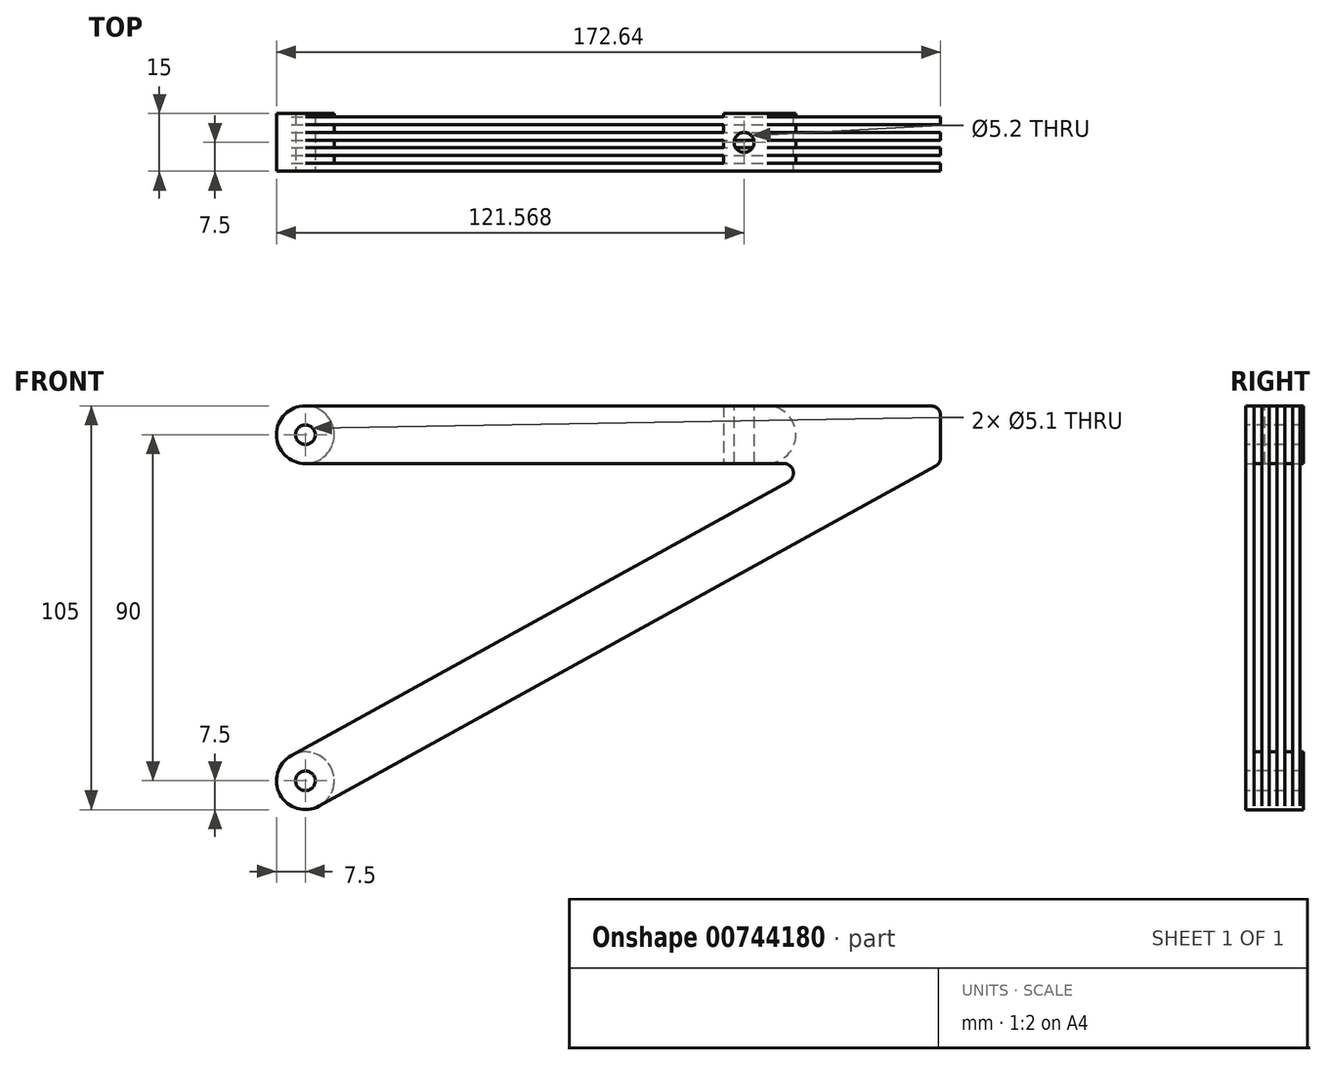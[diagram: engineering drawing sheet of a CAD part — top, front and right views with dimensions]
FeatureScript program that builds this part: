
annotation { "Feature Type Name" : "Feature", "Feature Type Description" : "" }
export const myFeature = defineFeature(function(context is Context, id is Id, definition is map)
    precondition{}
    {
        {
            var Q0;
            Q0=qCreatedBy(makeId("Front.planeOp"),FACE);
            var sketch = newSketch(context, id + "F0", { "sketchPlane" : qUnion([Q0])});
            skLineSegment(sketch, "E0", {"start": v(0, 120) * mm, "end": v(0, 30) * mm, "construction": true});
            skCircle(sketch, "E1", {"center": v(0, 120) * mm, "radius": 7.5 * mm});
            skCircle(sketch, "E2", {"center": v(0, 30) * mm, "radius": 7.5 * mm});
            skLineSegment(sketch, "E3", {"start": v(0, 127.5) * mm, "end": v(120, 127.5) * mm});
            skLineSegment(sketch, "E4", {"start": v(0, 112.5) * mm, "end": v(120, 112.5) * mm});
            skArc(sketch, "E5", {"start": v(120, 112.5) * mm, "mid": v(127.5, 120) * mm, "end": v(120, 127.5) * mm});
            skLineSegment(sketch, "E6", {"start": v(120, 127.5) * mm, "end": v(162.64, 127.5) * mm});
            skLineSegment(sketch, "E7", {"start": v(165.14, 125) * mm, "end": v(165.14, 113.98) * mm});
            skLineSegment(sketch, "E8", {"start": v(124.36, 112.5) * mm, "end": v(120, 112.5) * mm});
            skLineSegment(sketch, "E9", {"start": v(125.57, 107.81) * mm, "end": v(-3.62, 36.57) * mm});
            skLineSegment(sketch, "E10", {"start": v(3.62, 23.43) * mm, "end": v(163.85, 111.79) * mm});
            skPoint(sketch, "E11.visualSharp", {"position": v(165.14, 127.5) * mm});
            skArc(sketch, "E11.filletArc", {"start": v(165.14, 125) * mm, "mid": v(164.4, 126.77) * mm, "end": v(162.64, 127.5) * mm});
            skPoint(sketch, "E12.visualSharp", {"position": v(165.14, 112.5) * mm});
            skArc(sketch, "E12.filletArc", {"start": v(163.85, 111.79) * mm, "mid": v(164.8, 112.7) * mm, "end": v(165.14, 113.98) * mm});
            skPoint(sketch, "E13.visualSharp", {"position": v(134.08, 112.5) * mm});
            skArc(sketch, "E13.filletArc", {"start": v(125.57, 107.81) * mm, "mid": v(126.79, 110.62) * mm, "end": v(124.36, 112.5) * mm});
            skLineSegment(sketch, "E14", {"start": v(108.79, 127.5) * mm, "end": v(108.79, 112.5) * mm});
            skSolve(sketch);
        }
        {
            var Q0;
            {var subQ0=sQuery(id+"F0.wireOp",EDGE,"E3");Q0=makeQuery(id+"F0.imprint","IMPRINT",FACE,{"disambiguationData":[TD([[makeQuery(id+"F0.imprint","IMPRINT",EDGE,{"derivedFrom":subQ0}),-1.0]])]});}
            var Q1;
            {var subQ0=sQuery(id+"F0.wireOp",EDGE,"E1");var subQ1=makeQuery(id+"F0.imprint","INTERSECT",VERTEX,{"derivedFrom":[subQ0,sQuery(id+"F0.wireOp",EDGE,"E3")]});Q1=makeQuery(id+"F0.imprint","IMPRINT",FACE,{"disambiguationData":[TD([[makeQuery(id+"F0.imprint","IMPRINT",EDGE,{"disambiguationData":[TD([[subQ1,-1.0]])],"derivedFrom":subQ0}),1.0]])]});}
            var Q2;
            {var subQ3=sQuery(id+"F0.wireOp",EDGE,"E6");Q2=makeQuery(id+"F0.imprint","IMPRINT",FACE,{"disambiguationData":[TD([[makeQuery(id+"F0.imprint","IMPRINT",EDGE,{"derivedFrom":subQ3}),-1.0]])]});}
            var Q3;
            {var subQ0=sQuery(id+"F0.wireOp",EDGE,"E9");Q3=makeQuery(id+"F0.imprint","IMPRINT",FACE,{"disambiguationData":[TD([[makeQuery(id+"F0.imprint","IMPRINT",EDGE,{"derivedFrom":subQ0}),1.0]])]});}
            var Q4;
            {var subQ0=sQuery(id+"F0.wireOp",EDGE,"E2");var subQ1=makeQuery(id+"F0.imprint","INTERSECT",VERTEX,{"derivedFrom":[subQ0,sQuery(id+"F0.wireOp",EDGE,"E9")]});Q4=makeQuery(id+"F0.imprint","IMPRINT",FACE,{"disambiguationData":[TD([[makeQuery(id+"F0.imprint","IMPRINT",EDGE,{"disambiguationData":[TD([[subQ1,-1.0]])],"derivedFrom":subQ0}),1.0]])]});}
            var Q5;
            {var subQ0=sQuery(id+"F0.wireOp",EDGE,"E5");var subQ1=makeQuery(id+"F0.imprint","INTERSECT",VERTEX,{"derivedFrom":[sQuery(id+"F0.wireOp",EDGE,"E3"),subQ0,sQuery(id+"F0.wireOp",EDGE,"E6")]});Q5=makeQuery(id+"F0.imprint","IMPRINT",FACE,{"disambiguationData":[TD([[makeQuery(id+"F0.imprint","IMPRINT",EDGE,{"disambiguationData":[TD([[subQ1,-1.0]])],"derivedFrom":subQ0}),1.0]])]});}
            extrude(context, id + "F1", {"entities" : qUnion([Q0, Q1, Q2, Q3, Q4, Q5]), "depth" : 15 * mm, "offsetDistance" : 25 * mm, "symmetric" : true});
        }
        {
            var Q0;
            Q0=qCreatedBy(makeId("Top.planeOp"),FACE);
            var sketch = newSketch(context, id + "F2", { "sketchPlane" : qUnion([Q0])});
            skLineSegment(sketch, "E15.bottom", {"start": v(-14.24, 8.62) * mm, "end": v(173.7, 8.62) * mm});
            skLineSegment(sketch, "E15.top", {"start": v(-14.24, 6.62) * mm, "end": v(173.7, 6.62) * mm});
            skLineSegment(sketch, "E15.left", {"start": v(-14.24, 8.62) * mm, "end": v(-14.24, 6.62) * mm});
            skLineSegment(sketch, "E15.right", {"start": v(173.7, 8.62) * mm, "end": v(173.7, 6.62) * mm});
            skLineSegment(sketch, "E16.1.0.0", {"start": v(10.76, 8.62) * mm, "end": v(198.7, 8.62) * mm});
            skLineSegment(sketch, "E16.1.0.1", {"start": v(10.76, 6.62) * mm, "end": v(198.7, 6.62) * mm});
            skLineSegment(sketch, "E16.1.0.2", {"start": v(198.7, 8.62) * mm, "end": v(198.7, 6.62) * mm});
            skLineSegment(sketch, "E16.1.0.3", {"start": v(10.76, 8.62) * mm, "end": v(10.76, 6.62) * mm});
            skLineSegment(sketch, "E16.2.0.0", {"start": v(35.76, 8.62) * mm, "end": v(223.7, 8.62) * mm});
            skLineSegment(sketch, "E16.2.0.1", {"start": v(35.76, 6.62) * mm, "end": v(223.7, 6.62) * mm});
            skLineSegment(sketch, "E16.2.0.2", {"start": v(223.7, 8.62) * mm, "end": v(223.7, 6.62) * mm});
            skLineSegment(sketch, "E16.2.0.3", {"start": v(35.76, 8.62) * mm, "end": v(35.76, 6.62) * mm});
            skLineSegment(sketch, "E16.direction1", {"start": v(-14.24, 6.62) * mm, "end": v(10.76, 6.62) * mm, "construction": true});
            skLineSegment(sketch, "E17.0.1.0", {"start": v(10.76, 2.62) * mm, "end": v(198.7, 2.62) * mm});
            skLineSegment(sketch, "E17.0.1.1", {"start": v(35.76, 4.62) * mm, "end": v(223.7, 4.62) * mm});
            skLineSegment(sketch, "E17.0.1.2", {"start": v(-14.24, 4.62) * mm, "end": v(173.7, 4.62) * mm});
            skLineSegment(sketch, "E17.0.1.3", {"start": v(-14.24, 2.62) * mm, "end": v(10.76, 2.62) * mm, "construction": true});
            skLineSegment(sketch, "E17.0.1.4", {"start": v(10.76, 4.62) * mm, "end": v(198.7, 4.62) * mm});
            skLineSegment(sketch, "E17.0.1.5", {"start": v(35.76, 2.62) * mm, "end": v(223.7, 2.62) * mm});
            skLineSegment(sketch, "E17.0.1.6", {"start": v(-14.24, 2.62) * mm, "end": v(173.7, 2.62) * mm});
            skLineSegment(sketch, "E17.0.1.7", {"start": v(35.76, 4.62) * mm, "end": v(35.76, 2.62) * mm});
            skLineSegment(sketch, "E17.0.1.8", {"start": v(-14.24, 4.62) * mm, "end": v(-14.24, 2.62) * mm});
            skLineSegment(sketch, "E17.0.1.9", {"start": v(223.7, 4.62) * mm, "end": v(223.7, 2.62) * mm});
            skLineSegment(sketch, "E17.0.1.10", {"start": v(198.7, 4.62) * mm, "end": v(198.7, 2.62) * mm});
            skLineSegment(sketch, "E17.0.1.11", {"start": v(173.7, 4.62) * mm, "end": v(173.7, 2.62) * mm});
            skLineSegment(sketch, "E17.0.1.12", {"start": v(10.76, 4.62) * mm, "end": v(10.76, 2.62) * mm});
            skLineSegment(sketch, "E17.0.2.0", {"start": v(10.76, -1.38) * mm, "end": v(198.7, -1.38) * mm});
            skLineSegment(sketch, "E17.0.2.1", {"start": v(35.76, 0.62) * mm, "end": v(223.7, 0.62) * mm});
            skLineSegment(sketch, "E17.0.2.2", {"start": v(-14.24, 0.62) * mm, "end": v(173.7, 0.62) * mm});
            skLineSegment(sketch, "E17.0.2.3", {"start": v(-14.24, -1.38) * mm, "end": v(10.76, -1.38) * mm, "construction": true});
            skLineSegment(sketch, "E17.0.2.4", {"start": v(10.76, 0.62) * mm, "end": v(198.7, 0.62) * mm});
            skLineSegment(sketch, "E17.0.2.5", {"start": v(35.76, -1.38) * mm, "end": v(223.7, -1.38) * mm});
            skLineSegment(sketch, "E17.0.2.6", {"start": v(-14.24, -1.38) * mm, "end": v(173.7, -1.38) * mm});
            skLineSegment(sketch, "E17.0.2.7", {"start": v(35.76, 0.62) * mm, "end": v(35.76, -1.38) * mm});
            skLineSegment(sketch, "E17.0.2.8", {"start": v(-14.24, 0.62) * mm, "end": v(-14.24, -1.38) * mm});
            skLineSegment(sketch, "E17.0.2.9", {"start": v(223.7, 0.62) * mm, "end": v(223.7, -1.38) * mm});
            skLineSegment(sketch, "E17.0.2.10", {"start": v(198.7, 0.62) * mm, "end": v(198.7, -1.38) * mm});
            skLineSegment(sketch, "E17.0.2.11", {"start": v(173.7, 0.62) * mm, "end": v(173.7, -1.38) * mm});
            skLineSegment(sketch, "E17.0.2.12", {"start": v(10.76, 0.62) * mm, "end": v(10.76, -1.38) * mm});
            skLineSegment(sketch, "E17.0.3.0", {"start": v(10.76, -5.38) * mm, "end": v(198.7, -5.38) * mm});
            skLineSegment(sketch, "E17.0.3.1", {"start": v(35.76, -3.38) * mm, "end": v(223.7, -3.38) * mm});
            skLineSegment(sketch, "E17.0.3.2", {"start": v(-14.24, -3.38) * mm, "end": v(173.7, -3.38) * mm});
            skLineSegment(sketch, "E17.0.3.3", {"start": v(-14.24, -5.38) * mm, "end": v(10.76, -5.38) * mm, "construction": true});
            skLineSegment(sketch, "E17.0.3.4", {"start": v(10.76, -3.38) * mm, "end": v(198.7, -3.38) * mm});
            skLineSegment(sketch, "E17.0.3.5", {"start": v(35.76, -5.38) * mm, "end": v(223.7, -5.38) * mm});
            skLineSegment(sketch, "E17.0.3.6", {"start": v(-14.24, -5.38) * mm, "end": v(173.7, -5.38) * mm});
            skLineSegment(sketch, "E17.0.3.7", {"start": v(35.76, -3.38) * mm, "end": v(35.76, -5.38) * mm});
            skLineSegment(sketch, "E17.0.3.8", {"start": v(-14.24, -3.38) * mm, "end": v(-14.24, -5.38) * mm});
            skLineSegment(sketch, "E17.0.3.9", {"start": v(223.7, -3.38) * mm, "end": v(223.7, -5.38) * mm});
            skLineSegment(sketch, "E17.0.3.10", {"start": v(198.7, -3.38) * mm, "end": v(198.7, -5.38) * mm});
            skLineSegment(sketch, "E17.0.3.11", {"start": v(173.7, -3.38) * mm, "end": v(173.7, -5.38) * mm});
            skLineSegment(sketch, "E17.0.3.12", {"start": v(10.76, -3.38) * mm, "end": v(10.76, -5.38) * mm});
            skLineSegment(sketch, "E17.1.0.1", {"start": v(60.76, 8.62) * mm, "end": v(248.7, 8.62) * mm});
            skLineSegment(sketch, "E17.1.0.3", {"start": v(10.76, 6.62) * mm, "end": v(35.76, 6.62) * mm, "construction": true});
            skLineSegment(sketch, "E17.1.0.5", {"start": v(60.76, 6.62) * mm, "end": v(248.7, 6.62) * mm});
            skLineSegment(sketch, "E17.1.0.7", {"start": v(60.76, 8.62) * mm, "end": v(60.76, 6.62) * mm});
            skLineSegment(sketch, "E17.1.0.9", {"start": v(248.7, 8.62) * mm, "end": v(248.7, 6.62) * mm});
            skLineSegment(sketch, "E17.1.1.0", {"start": v(35.76, 2.62) * mm, "end": v(223.7, 2.62) * mm});
            skLineSegment(sketch, "E17.1.1.1", {"start": v(60.76, 4.62) * mm, "end": v(248.7, 4.62) * mm});
            skLineSegment(sketch, "E17.1.1.2", {"start": v(10.76, 4.62) * mm, "end": v(198.7, 4.62) * mm});
            skLineSegment(sketch, "E17.1.1.3", {"start": v(10.76, 2.62) * mm, "end": v(35.76, 2.62) * mm, "construction": true});
            skLineSegment(sketch, "E17.1.1.4", {"start": v(35.76, 4.62) * mm, "end": v(223.7, 4.62) * mm});
            skLineSegment(sketch, "E17.1.1.5", {"start": v(60.76, 2.62) * mm, "end": v(248.7, 2.62) * mm});
            skLineSegment(sketch, "E17.1.1.6", {"start": v(10.76, 2.62) * mm, "end": v(198.7, 2.62) * mm});
            skLineSegment(sketch, "E17.1.1.7", {"start": v(60.76, 4.62) * mm, "end": v(60.76, 2.62) * mm});
            skLineSegment(sketch, "E17.1.1.8", {"start": v(10.76, 4.62) * mm, "end": v(10.76, 2.62) * mm});
            skLineSegment(sketch, "E17.1.1.9", {"start": v(248.7, 4.62) * mm, "end": v(248.7, 2.62) * mm});
            skLineSegment(sketch, "E17.1.1.10", {"start": v(223.7, 4.62) * mm, "end": v(223.7, 2.62) * mm});
            skLineSegment(sketch, "E17.1.1.11", {"start": v(198.7, 4.62) * mm, "end": v(198.7, 2.62) * mm});
            skLineSegment(sketch, "E17.1.1.12", {"start": v(35.76, 4.62) * mm, "end": v(35.76, 2.62) * mm});
            skLineSegment(sketch, "E17.1.2.0", {"start": v(35.76, -1.38) * mm, "end": v(223.7, -1.38) * mm});
            skLineSegment(sketch, "E17.1.2.1", {"start": v(60.76, 0.62) * mm, "end": v(248.7, 0.62) * mm});
            skLineSegment(sketch, "E17.1.2.2", {"start": v(10.76, 0.62) * mm, "end": v(198.7, 0.62) * mm});
            skLineSegment(sketch, "E17.1.2.3", {"start": v(10.76, -1.38) * mm, "end": v(35.76, -1.38) * mm, "construction": true});
            skLineSegment(sketch, "E17.1.2.4", {"start": v(35.76, 0.62) * mm, "end": v(223.7, 0.62) * mm});
            skLineSegment(sketch, "E17.1.2.5", {"start": v(60.76, -1.38) * mm, "end": v(248.7, -1.38) * mm});
            skLineSegment(sketch, "E17.1.2.6", {"start": v(10.76, -1.38) * mm, "end": v(198.7, -1.38) * mm});
            skLineSegment(sketch, "E17.1.2.7", {"start": v(60.76, 0.62) * mm, "end": v(60.76, -1.38) * mm});
            skLineSegment(sketch, "E17.1.2.8", {"start": v(10.76, 0.62) * mm, "end": v(10.76, -1.38) * mm});
            skLineSegment(sketch, "E17.1.2.9", {"start": v(248.7, 0.62) * mm, "end": v(248.7, -1.38) * mm});
            skLineSegment(sketch, "E17.1.2.10", {"start": v(223.7, 0.62) * mm, "end": v(223.7, -1.38) * mm});
            skLineSegment(sketch, "E17.1.2.11", {"start": v(198.7, 0.62) * mm, "end": v(198.7, -1.38) * mm});
            skLineSegment(sketch, "E17.1.2.12", {"start": v(35.76, 0.62) * mm, "end": v(35.76, -1.38) * mm});
            skLineSegment(sketch, "E17.1.3.0", {"start": v(35.76, -5.38) * mm, "end": v(223.7, -5.38) * mm});
            skLineSegment(sketch, "E17.1.3.1", {"start": v(60.76, -3.38) * mm, "end": v(248.7, -3.38) * mm});
            skLineSegment(sketch, "E17.1.3.2", {"start": v(10.76, -3.38) * mm, "end": v(198.7, -3.38) * mm});
            skLineSegment(sketch, "E17.1.3.3", {"start": v(10.76, -5.38) * mm, "end": v(35.76, -5.38) * mm, "construction": true});
            skLineSegment(sketch, "E17.1.3.4", {"start": v(35.76, -3.38) * mm, "end": v(223.7, -3.38) * mm});
            skLineSegment(sketch, "E17.1.3.5", {"start": v(60.76, -5.38) * mm, "end": v(248.7, -5.38) * mm});
            skLineSegment(sketch, "E17.1.3.6", {"start": v(10.76, -5.38) * mm, "end": v(198.7, -5.38) * mm});
            skLineSegment(sketch, "E17.1.3.7", {"start": v(60.76, -3.38) * mm, "end": v(60.76, -5.38) * mm});
            skLineSegment(sketch, "E17.1.3.8", {"start": v(10.76, -3.38) * mm, "end": v(10.76, -5.38) * mm});
            skLineSegment(sketch, "E17.1.3.9", {"start": v(248.7, -3.38) * mm, "end": v(248.7, -5.38) * mm});
            skLineSegment(sketch, "E17.1.3.10", {"start": v(223.7, -3.38) * mm, "end": v(223.7, -5.38) * mm});
            skLineSegment(sketch, "E17.1.3.11", {"start": v(198.7, -3.38) * mm, "end": v(198.7, -5.38) * mm});
            skLineSegment(sketch, "E17.1.3.12", {"start": v(35.76, -3.38) * mm, "end": v(35.76, -5.38) * mm});
            skLineSegment(sketch, "E17.2.0.0", {"start": v(60.76, 6.62) * mm, "end": v(248.7, 6.62) * mm});
            skLineSegment(sketch, "E17.2.0.1", {"start": v(85.76, 8.62) * mm, "end": v(273.7, 8.62) * mm});
            skLineSegment(sketch, "E17.2.0.3", {"start": v(35.76, 6.62) * mm, "end": v(60.76, 6.62) * mm, "construction": true});
            skLineSegment(sketch, "E17.2.0.4", {"start": v(60.76, 8.62) * mm, "end": v(248.7, 8.62) * mm});
            skLineSegment(sketch, "E17.2.0.5", {"start": v(85.76, 6.62) * mm, "end": v(273.7, 6.62) * mm});
            skLineSegment(sketch, "E17.2.0.7", {"start": v(85.76, 8.62) * mm, "end": v(85.76, 6.62) * mm});
            skLineSegment(sketch, "E17.2.0.9", {"start": v(273.7, 8.62) * mm, "end": v(273.7, 6.62) * mm});
            skLineSegment(sketch, "E17.2.0.10", {"start": v(248.7, 8.62) * mm, "end": v(248.7, 6.62) * mm});
            skLineSegment(sketch, "E17.2.0.12", {"start": v(60.76, 8.62) * mm, "end": v(60.76, 6.62) * mm});
            skLineSegment(sketch, "E17.2.1.0", {"start": v(60.76, 2.62) * mm, "end": v(248.7, 2.62) * mm});
            skLineSegment(sketch, "E17.2.1.1", {"start": v(85.76, 4.62) * mm, "end": v(273.7, 4.62) * mm});
            skLineSegment(sketch, "E17.2.1.2", {"start": v(35.76, 4.62) * mm, "end": v(223.7, 4.62) * mm});
            skLineSegment(sketch, "E17.2.1.3", {"start": v(35.76, 2.62) * mm, "end": v(60.76, 2.62) * mm, "construction": true});
            skLineSegment(sketch, "E17.2.1.4", {"start": v(60.76, 4.62) * mm, "end": v(248.7, 4.62) * mm});
            skLineSegment(sketch, "E17.2.1.5", {"start": v(85.76, 2.62) * mm, "end": v(273.7, 2.62) * mm});
            skLineSegment(sketch, "E17.2.1.6", {"start": v(35.76, 2.62) * mm, "end": v(223.7, 2.62) * mm});
            skLineSegment(sketch, "E17.2.1.7", {"start": v(85.76, 4.62) * mm, "end": v(85.76, 2.62) * mm});
            skLineSegment(sketch, "E17.2.1.8", {"start": v(35.76, 4.62) * mm, "end": v(35.76, 2.62) * mm});
            skLineSegment(sketch, "E17.2.1.9", {"start": v(273.7, 4.62) * mm, "end": v(273.7, 2.62) * mm});
            skLineSegment(sketch, "E17.2.1.10", {"start": v(248.7, 4.62) * mm, "end": v(248.7, 2.62) * mm});
            skLineSegment(sketch, "E17.2.1.11", {"start": v(223.7, 4.62) * mm, "end": v(223.7, 2.62) * mm});
            skLineSegment(sketch, "E17.2.1.12", {"start": v(60.76, 4.62) * mm, "end": v(60.76, 2.62) * mm});
            skLineSegment(sketch, "E17.2.2.0", {"start": v(60.76, -1.38) * mm, "end": v(248.7, -1.38) * mm});
            skLineSegment(sketch, "E17.2.2.1", {"start": v(85.76, 0.62) * mm, "end": v(273.7, 0.62) * mm});
            skLineSegment(sketch, "E17.2.2.2", {"start": v(35.76, 0.62) * mm, "end": v(223.7, 0.62) * mm});
            skLineSegment(sketch, "E17.2.2.3", {"start": v(35.76, -1.38) * mm, "end": v(60.76, -1.38) * mm, "construction": true});
            skLineSegment(sketch, "E17.2.2.4", {"start": v(60.76, 0.62) * mm, "end": v(248.7, 0.62) * mm});
            skLineSegment(sketch, "E17.2.2.5", {"start": v(85.76, -1.38) * mm, "end": v(273.7, -1.38) * mm});
            skLineSegment(sketch, "E17.2.2.6", {"start": v(35.76, -1.38) * mm, "end": v(223.7, -1.38) * mm});
            skLineSegment(sketch, "E17.2.2.7", {"start": v(85.76, 0.62) * mm, "end": v(85.76, -1.38) * mm});
            skLineSegment(sketch, "E17.2.2.8", {"start": v(35.76, 0.62) * mm, "end": v(35.76, -1.38) * mm});
            skLineSegment(sketch, "E17.2.2.9", {"start": v(273.7, 0.62) * mm, "end": v(273.7, -1.38) * mm});
            skLineSegment(sketch, "E17.2.2.10", {"start": v(248.7, 0.62) * mm, "end": v(248.7, -1.38) * mm});
            skLineSegment(sketch, "E17.2.2.11", {"start": v(223.7, 0.62) * mm, "end": v(223.7, -1.38) * mm});
            skLineSegment(sketch, "E17.2.2.12", {"start": v(60.76, 0.62) * mm, "end": v(60.76, -1.38) * mm});
            skLineSegment(sketch, "E17.2.3.0", {"start": v(60.76, -5.38) * mm, "end": v(248.7, -5.38) * mm});
            skLineSegment(sketch, "E17.2.3.1", {"start": v(85.76, -3.38) * mm, "end": v(273.7, -3.38) * mm});
            skLineSegment(sketch, "E17.2.3.2", {"start": v(35.76, -3.38) * mm, "end": v(223.7, -3.38) * mm});
            skLineSegment(sketch, "E17.2.3.3", {"start": v(35.76, -5.38) * mm, "end": v(60.76, -5.38) * mm, "construction": true});
            skLineSegment(sketch, "E17.2.3.4", {"start": v(60.76, -3.38) * mm, "end": v(248.7, -3.38) * mm});
            skLineSegment(sketch, "E17.2.3.5", {"start": v(85.76, -5.38) * mm, "end": v(273.7, -5.38) * mm});
            skLineSegment(sketch, "E17.2.3.6", {"start": v(35.76, -5.38) * mm, "end": v(223.7, -5.38) * mm});
            skLineSegment(sketch, "E17.2.3.7", {"start": v(85.76, -3.38) * mm, "end": v(85.76, -5.38) * mm});
            skLineSegment(sketch, "E17.2.3.8", {"start": v(35.76, -3.38) * mm, "end": v(35.76, -5.38) * mm});
            skLineSegment(sketch, "E17.2.3.9", {"start": v(273.7, -3.38) * mm, "end": v(273.7, -5.38) * mm});
            skLineSegment(sketch, "E17.2.3.10", {"start": v(248.7, -3.38) * mm, "end": v(248.7, -5.38) * mm});
            skLineSegment(sketch, "E17.2.3.11", {"start": v(223.7, -3.38) * mm, "end": v(223.7, -5.38) * mm});
            skLineSegment(sketch, "E17.2.3.12", {"start": v(60.76, -3.38) * mm, "end": v(60.76, -5.38) * mm});
            skLineSegment(sketch, "E17.direction2", {"start": v(-14.24, 6.62) * mm, "end": v(-14.24, 2.62) * mm, "construction": true});
            skSolve(sketch);
        }
        {
            var Q0;
            {var subQ4=sQuery(id+"F2.wireOp",EDGE,"E17.0.3.6");var subQ7=sQuery(id+"F2.wireOp",EDGE,"E17.0.3.7");var subQ11=makeQuery(id+"F2.imprint","IMPRINT",EDGE,{"derivedFrom":subQ7});var subQ14=sQuery(id+"F2.wireOp",EDGE,"E17.0.3.11");var subQ19=makeQuery(id+"F2.imprint","IMPRINT",EDGE,{"derivedFrom":subQ14});var subQ20=sQuery(id+"F2.wireOp",EDGE,"E17.1.3.7");var subQ22=makeQuery(id+"F2.imprint","IMPRINT",EDGE,{"derivedFrom":subQ20});var subQ24=sQuery(id+"F2.wireOp",EDGE,"E17.0.3.10");var subQ25=sQuery(id+"F2.wireOp",EDGE,"E17.0.3.5");var subQ27=makeQuery(id+"F2.imprint","IMPRINT",EDGE,{"derivedFrom":subQ24});var subQ29=sQuery(id+"F2.wireOp",EDGE,"E17.0.3.9");var subQ30=makeQuery(id+"F2.imprint","IMPRINT",EDGE,{"derivedFrom":subQ29});var subQ31=makeQuery(id+"F2.imprint","IMPRINT",EDGE,{"derivedFrom":sQuery(id+"F2.wireOp",EDGE,"E17.1.3.9")});var subQ33=sQuery(id+"F2.wireOp",EDGE,"E17.0.2.9");var subQ35=sQuery(id+"F2.wireOp",EDGE,"E17.0.2.10");var subQ37=sQuery(id+"F2.wireOp",EDGE,"E17.0.2.5");var subQ38=makeQuery(id+"F2.imprint","IMPRINT",EDGE,{"derivedFrom":subQ35});var subQ39=makeQuery(id+"F2.imprint","IMPRINT",EDGE,{"derivedFrom":subQ33});var subQ41=sQuery(id+"F2.wireOp",EDGE,"E17.0.2.11");var subQ44=makeQuery(id+"F2.imprint","IMPRINT",EDGE,{"derivedFrom":subQ41});var subQ45=makeQuery(id+"F2.imprint","IMPRINT",EDGE,{"derivedFrom":sQuery(id+"F2.wireOp",EDGE,"E17.1.2.9")});var subQ47=sQuery(id+"F2.wireOp",EDGE,"E17.0.2.6");var subQ48=sQuery(id+"F2.wireOp",EDGE,"E17.0.2.7");var subQ53=makeQuery(id+"F2.imprint","IMPRINT",EDGE,{"derivedFrom":subQ48});var subQ58=sQuery(id+"F2.wireOp",EDGE,"E17.1.2.7");var subQ62=makeQuery(id+"F2.imprint","IMPRINT",EDGE,{"derivedFrom":subQ58});var subQ65=sQuery(id+"F2.wireOp",EDGE,"E17.0.1.9");var subQ67=sQuery(id+"F2.wireOp",EDGE,"E17.0.1.10");var subQ69=sQuery(id+"F2.wireOp",EDGE,"E17.0.1.5");var subQ70=makeQuery(id+"F2.imprint","IMPRINT",EDGE,{"derivedFrom":subQ67});var subQ71=makeQuery(id+"F2.imprint","IMPRINT",EDGE,{"derivedFrom":subQ65});var subQ73=sQuery(id+"F2.wireOp",EDGE,"E17.0.1.11");var subQ76=makeQuery(id+"F2.imprint","IMPRINT",EDGE,{"derivedFrom":subQ73});var subQ81=makeQuery(id+"F2.imprint","IMPRINT",EDGE,{"derivedFrom":sQuery(id+"F2.wireOp",EDGE,"E17.1.1.9")});var subQ83=sQuery(id+"F2.wireOp",EDGE,"E17.0.1.6");var subQ84=sQuery(id+"F2.wireOp",EDGE,"E17.0.1.7");var subQ89=makeQuery(id+"F2.imprint","IMPRINT",EDGE,{"derivedFrom":subQ84});var subQ92=sQuery(id+"F2.wireOp",EDGE,"E17.1.1.7");var subQ95=makeQuery(id+"F2.imprint","IMPRINT",EDGE,{"derivedFrom":subQ92});var subQ99=sQuery(id+"F2.wireOp",EDGE,"E17.1.0.7");var subQ104=makeQuery(id+"F2.imprint","IMPRINT",EDGE,{"derivedFrom":subQ99});var subQ107=sQuery(id+"F2.wireOp",EDGE,"E15.right");var subQ109=makeQuery(id+"F2.imprint","IMPRINT",EDGE,{"derivedFrom":subQ107});var subQ110=makeQuery(id+"F2.imprint","IMPRINT",EDGE,{"derivedFrom":sQuery(id+"F2.wireOp",EDGE,"E16.1.0.2")});var subQ111=makeQuery(id+"F2.imprint","IMPRINT",EDGE,{"derivedFrom":sQuery(id+"F2.wireOp",EDGE,"E16.2.0.2")});var subQ112=makeQuery(id+"F2.imprint","IMPRINT",EDGE,{"derivedFrom":sQuery(id+"F2.wireOp",EDGE,"E17.1.0.9")});var subQ113=sQuery(id+"F2.wireOp",EDGE,"E16.2.0.3");var subQ116=makeQuery(id+"F2.imprint","IMPRINT",EDGE,{"derivedFrom":subQ113});var subQ117=sQuery(id+"F2.wireOp",EDGE,"E16.1.0.3");var subQ119=sQuery(id+"F2.wireOp",EDGE,"E15.left");var subQ121=makeQuery(id+"F2.imprint","IMPRINT",EDGE,{"derivedFrom":subQ117});Q0=qUnion([makeQuery(id+"F2.imprint","IMPRINT",FACE,{"disambiguationData":[TD([[subQ121,1.0]])]}),makeQuery(id+"F2.imprint","IMPRINT",FACE,{"disambiguationData":[TD([[makeQuery(id+"F2.imprint","IMPRINT",EDGE,{"derivedFrom":subQ119}),1.0]])]}),makeQuery(id+"F2.imprint","IMPRINT",FACE,{"disambiguationData":[TD([[subQ112,1.0]])]}),makeQuery(id+"F2.imprint","IMPRINT",FACE,{"disambiguationData":[TD([[subQ110,1.0]])]}),makeQuery(id+"F2.imprint","IMPRINT",FACE,{"disambiguationData":[TD([[subQ116,1.0]])]}),makeQuery(id+"F2.imprint","IMPRINT",FACE,{"disambiguationData":[TD([[subQ111,1.0]])]}),makeQuery(id+"F2.imprint","IMPRINT",FACE,{"disambiguationData":[TD([[subQ109,1.0]])]}),makeQuery(id+"F2.imprint","IMPRINT",FACE,{"disambiguationData":[TD([[subQ109,-1.0]])]}),makeQuery(id+"F2.imprint","IMPRINT",FACE,{"disambiguationData":[TD([[subQ104,1.0]])]}),makeQuery(id+"F2.imprint","IMPRINT",FACE,{"disambiguationData":[TD([[subQ89,1.0]])]}),makeQuery(id+"F2.imprint","IMPRINT",FACE,{"disambiguationData":[TD([[subQ95,1.0]])]}),makeQuery(id+"F2.imprint","IMPRINT",FACE,{"disambiguationData":[TD([[makeQuery(id+"F2.imprint","IMPRINT",EDGE,{"derivedFrom":subQ83}),1.0]])]}),makeQuery(id+"F2.imprint","IMPRINT",FACE,{"disambiguationData":[TD([[subQ81,1.0]])]}),makeQuery(id+"F2.imprint","IMPRINT",FACE,{"disambiguationData":[TD([[subQ89,-1.0]])]}),makeQuery(id+"F2.imprint","IMPRINT",FACE,{"disambiguationData":[TD([[subQ71,1.0]])]}),makeQuery(id+"F2.imprint","IMPRINT",FACE,{"disambiguationData":[TD([[subQ76,-1.0]])]}),makeQuery(id+"F2.imprint","IMPRINT",FACE,{"disambiguationData":[TD([[subQ70,-1.0]])]}),makeQuery(id+"F2.imprint","IMPRINT",FACE,{"disambiguationData":[TD([[makeQuery(id+"F2.imprint","IMPRINT",EDGE,{"derivedFrom":subQ69}),1.0]])]}),makeQuery(id+"F2.imprint","IMPRINT",FACE,{"disambiguationData":[TD([[subQ45,1.0]])]}),makeQuery(id+"F2.imprint","IMPRINT",FACE,{"disambiguationData":[TD([[subQ44,-1.0]])]}),makeQuery(id+"F2.imprint","IMPRINT",FACE,{"disambiguationData":[TD([[subQ53,1.0]])]}),makeQuery(id+"F2.imprint","IMPRINT",FACE,{"disambiguationData":[TD([[subQ62,1.0]])]}),makeQuery(id+"F2.imprint","IMPRINT",FACE,{"disambiguationData":[TD([[makeQuery(id+"F2.imprint","IMPRINT",EDGE,{"derivedFrom":subQ47}),1.0]])]}),makeQuery(id+"F2.imprint","IMPRINT",FACE,{"disambiguationData":[TD([[subQ53,-1.0]])]}),makeQuery(id+"F2.imprint","IMPRINT",FACE,{"disambiguationData":[TD([[subQ39,1.0]])]}),makeQuery(id+"F2.imprint","IMPRINT",FACE,{"disambiguationData":[TD([[subQ38,-1.0]])]}),makeQuery(id+"F2.imprint","IMPRINT",FACE,{"disambiguationData":[TD([[makeQuery(id+"F2.imprint","IMPRINT",EDGE,{"derivedFrom":subQ37}),1.0]])]}),makeQuery(id+"F2.imprint","IMPRINT",FACE,{"disambiguationData":[TD([[subQ30,1.0]])]}),makeQuery(id+"F2.imprint","IMPRINT",FACE,{"disambiguationData":[TD([[subQ31,1.0]])]}),makeQuery(id+"F2.imprint","IMPRINT",FACE,{"disambiguationData":[TD([[makeQuery(id+"F2.imprint","IMPRINT",EDGE,{"derivedFrom":subQ25}),1.0]])]}),makeQuery(id+"F2.imprint","IMPRINT",FACE,{"disambiguationData":[TD([[subQ22,1.0]])]}),makeQuery(id+"F2.imprint","IMPRINT",FACE,{"disambiguationData":[TD([[subQ27,-1.0]])]}),makeQuery(id+"F2.imprint","IMPRINT",FACE,{"disambiguationData":[TD([[subQ11,1.0]])]}),makeQuery(id+"F2.imprint","IMPRINT",FACE,{"disambiguationData":[TD([[subQ19,-1.0]])]}),makeQuery(id+"F2.imprint","IMPRINT",FACE,{"disambiguationData":[TD([[subQ11,-1.0]])]}),makeQuery(id+"F2.imprint","IMPRINT",FACE,{"disambiguationData":[TD([[makeQuery(id+"F2.imprint","IMPRINT",EDGE,{"derivedFrom":subQ4}),1.0]])]})]);}
            extrude(context, id + "F3", {"entities" : qUnion([Q0]), "operationType" : NewBodyOperationType.REMOVE, "endBound" : BoundingType.THROUGH_ALL, "depth" : 25 * mm, "offsetDistance" : 25 * mm});
        }
        {
            var Q0;
            {var subQ0=sQuery(id+"F0.wireOp",EDGE,"E1");var subQ1=makeQuery(id+"F0.imprint","INTERSECT",VERTEX,{"derivedFrom":[subQ0,sQuery(id+"F0.wireOp",EDGE,"E3")]});Q0=makeQuery(id+"F0.imprint","IMPRINT",FACE,{"disambiguationData":[TD([[makeQuery(id+"F0.imprint","IMPRINT",EDGE,{"disambiguationData":[TD([[subQ1,-1.0]])],"derivedFrom":subQ0}),1.0]])]});}
            var Q1;
            {var subQ0=sQuery(id+"F0.wireOp",EDGE,"E5");var subQ1=makeQuery(id+"F0.imprint","INTERSECT",VERTEX,{"derivedFrom":[sQuery(id+"F0.wireOp",EDGE,"E3"),subQ0,sQuery(id+"F0.wireOp",EDGE,"E6")]});Q1=makeQuery(id+"F0.imprint","IMPRINT",FACE,{"disambiguationData":[TD([[makeQuery(id+"F0.imprint","IMPRINT",EDGE,{"disambiguationData":[TD([[subQ1,-1.0]])],"derivedFrom":subQ0}),1.0]])]});}
            var Q2;
            {var subQ0=sQuery(id+"F0.wireOp",EDGE,"E2");var subQ1=makeQuery(id+"F0.imprint","INTERSECT",VERTEX,{"derivedFrom":[subQ0,sQuery(id+"F0.wireOp",EDGE,"E9")]});Q2=makeQuery(id+"F0.imprint","IMPRINT",FACE,{"disambiguationData":[TD([[makeQuery(id+"F0.imprint","IMPRINT",EDGE,{"disambiguationData":[TD([[subQ1,-1.0]])],"derivedFrom":subQ0}),1.0]])]});}
            extrude(context, id + "F4", {"entities" : qUnion([Q0, Q1, Q2]), "operationType" : NewBodyOperationType.ADD, "depth" : 15 * mm, "offsetDistance" : 25 * mm, "symmetric" : true});
        }
        {
            var Q0;
            Q0=sQuery(id+"F0.wireOp",VERTEX,"E1.center");
            var Q1;
            Q1=sQuery(id+"F0.wireOp",VERTEX,"E0.end");
            var Q2;
            Q2=makeQuery(id+"F3.boolean.opBoolean","SPLIT",BODY,{"disambiguationData":[OD(0.0)],"derivedFrom":makeQuery(id+"F1.opExtrude","SWEPT_BODY",BODY,{"disambiguationData":[OSD([sQuery(id+"F0.wireOp",EDGE,"E1"),sQuery(id+"F0.wireOp",EDGE,"E2"),sQuery(id+"F0.wireOp",EDGE,"E3"),sQuery(id+"F0.wireOp",EDGE,"E4"),sQuery(id+"F0.wireOp",EDGE,"E6"),sQuery(id+"F0.wireOp",EDGE,"E7"),sQuery(id+"F0.wireOp",EDGE,"E8"),sQuery(id+"F0.wireOp",EDGE,"E9"),sQuery(id+"F0.wireOp",EDGE,"E10"),sQuery(id+"F0.wireOp",EDGE,"E11.filletArc"),sQuery(id+"F0.wireOp",EDGE,"E12.filletArc"),sQuery(id+"F0.wireOp",EDGE,"E13.filletArc")])]})});
            hole(context, id + "F5", {"style" : HoleStyle.SIMPLE, "endStyle" : HoleEndStyle.BLIND, "holeDiameter" : 3 * mm, "majorDiameter" : 5 * mm, "holeDepth" : 13.5 * mm, "isTappedThrough" : true, "tappedDepth" : 12 * mm, "tapClearance" : 3, "locations" : qUnion([Q0, Q1]), "scope" : qUnion([Q2])});
        }
        {
            var Q0;
            Q0=qCreatedBy(makeId("Front.planeOp"),FACE);
            var sketch = newSketch(context, id + "F6", { "sketchPlane" : qUnion([Q0])});
            skCircle(sketch, "E18", {"center": v(0, 120) * mm, "radius": 2.55 * mm});
            skCircle(sketch, "E19", {"center": v(0, 30) * mm, "radius": 2.55 * mm});
            skSolve(sketch);
        }
        {
            var Q0;
            {var subQ0=sQuery(id+"F0.wireOp",EDGE,"E3");var subQ5=sQuery(id+"F0.wireOp",EDGE,"E6");var subQ6=makeQuery(id+"F1.opExtrude","SWEPT_FACE",FACE,{"disambiguationData":[OSD([subQ0,subQ5])]});Q0=makeQuery(id+"F4.boolean.opBoolean","MERGE",FACE,{"derivedFrom":[makeQuery(id+"F3.boolean.opBoolean","SPLIT",FACE,{"disambiguationData":[TD([makeQuery(id+"F3.opExtrude","SWEPT_FACE",FACE,{"disambiguationData":[OSD([sQuery(id+"F2.wireOp",EDGE,"E17.0.3.0"),sQuery(id+"F2.wireOp",EDGE,"E17.0.3.5"),sQuery(id+"F2.wireOp",EDGE,"E17.0.3.6"),sQuery(id+"F2.wireOp",EDGE,"E17.1.3.5"),sQuery(id+"F2.wireOp",EDGE,"E17.2.3.5")])]})])],"derivedFrom":subQ6}),makeQuery(id+"F3.boolean.opBoolean","SPLIT",FACE,{"disambiguationData":[TD([makeQuery(id+"F3.opExtrude","SWEPT_FACE",FACE,{"disambiguationData":[OSD([sQuery(id+"F2.wireOp",EDGE,"E17.0.1.1"),sQuery(id+"F2.wireOp",EDGE,"E17.0.1.2"),sQuery(id+"F2.wireOp",EDGE,"E17.1.1.1"),sQuery(id+"F2.wireOp",EDGE,"E17.2.1.1")])]})])],"derivedFrom":subQ6}),makeQuery(id+"F3.boolean.opBoolean","SPLIT",FACE,{"disambiguationData":[TD([makeQuery(id+"F3.opExtrude","SWEPT_FACE",FACE,{"disambiguationData":[OSD([sQuery(id+"F2.wireOp",EDGE,"E17.0.2.1"),sQuery(id+"F2.wireOp",EDGE,"E17.0.2.2"),sQuery(id+"F2.wireOp",EDGE,"E17.1.2.1"),sQuery(id+"F2.wireOp",EDGE,"E17.2.2.1")])]})])],"derivedFrom":subQ6}),makeQuery(id+"F3.boolean.opBoolean","SPLIT",FACE,{"disambiguationData":[TD([makeQuery(id+"F3.opExtrude","SWEPT_FACE",FACE,{"disambiguationData":[OSD([sQuery(id+"F2.wireOp",EDGE,"E17.0.3.1"),sQuery(id+"F2.wireOp",EDGE,"E17.0.3.2"),sQuery(id+"F2.wireOp",EDGE,"E17.1.3.1"),sQuery(id+"F2.wireOp",EDGE,"E17.2.3.1")])]})])],"derivedFrom":subQ6}),makeQuery(id+"F4.opExtrude","SWEPT_FACE",FACE,{"disambiguationData":[OSD([subQ0])]})]});}
            var sketch = newSketch(context, id + "F7", { "sketchPlane" : qUnion([Q0])});
            skCircle(sketch, "E20", {"center": v(114.07, 0) * mm, "radius": 2.6 * mm});
            skSolve(sketch);
        }
        {
            var Q0;
            Q0 = qSketchRegion(id + "F7", true);
            var Q1;
            {var subQ0=sQuery(id+"F0.wireOp",EDGE,"E4");var subQ5=sQuery(id+"F0.wireOp",EDGE,"E8");var subQ6=makeQuery(id+"F1.opExtrude","SWEPT_FACE",FACE,{"disambiguationData":[OSD([subQ0,subQ5])]});Q1=makeQuery(id+"F4.boolean.opBoolean","MERGE",FACE,{"derivedFrom":[makeQuery(id+"F3.boolean.opBoolean","SPLIT",FACE,{"disambiguationData":[TD([makeQuery(id+"F3.opExtrude","SWEPT_FACE",FACE,{"disambiguationData":[OSD([sQuery(id+"F2.wireOp",EDGE,"E17.0.3.0"),sQuery(id+"F2.wireOp",EDGE,"E17.0.3.5"),sQuery(id+"F2.wireOp",EDGE,"E17.0.3.6"),sQuery(id+"F2.wireOp",EDGE,"E17.1.3.5"),sQuery(id+"F2.wireOp",EDGE,"E17.2.3.5")])]})])],"derivedFrom":subQ6}),makeQuery(id+"F3.boolean.opBoolean","SPLIT",FACE,{"disambiguationData":[TD([makeQuery(id+"F3.opExtrude","SWEPT_FACE",FACE,{"disambiguationData":[OSD([sQuery(id+"F2.wireOp",EDGE,"E17.0.1.1"),sQuery(id+"F2.wireOp",EDGE,"E17.0.1.2"),sQuery(id+"F2.wireOp",EDGE,"E17.1.1.1"),sQuery(id+"F2.wireOp",EDGE,"E17.2.1.1")])]})])],"derivedFrom":subQ6}),makeQuery(id+"F3.boolean.opBoolean","SPLIT",FACE,{"disambiguationData":[TD([makeQuery(id+"F3.opExtrude","SWEPT_FACE",FACE,{"disambiguationData":[OSD([sQuery(id+"F2.wireOp",EDGE,"E17.0.2.1"),sQuery(id+"F2.wireOp",EDGE,"E17.0.2.2"),sQuery(id+"F2.wireOp",EDGE,"E17.1.2.1"),sQuery(id+"F2.wireOp",EDGE,"E17.2.2.1")])]})])],"derivedFrom":subQ6}),makeQuery(id+"F3.boolean.opBoolean","SPLIT",FACE,{"disambiguationData":[TD([makeQuery(id+"F3.opExtrude","SWEPT_FACE",FACE,{"disambiguationData":[OSD([sQuery(id+"F2.wireOp",EDGE,"E17.0.3.1"),sQuery(id+"F2.wireOp",EDGE,"E17.0.3.2"),sQuery(id+"F2.wireOp",EDGE,"E17.1.3.1"),sQuery(id+"F2.wireOp",EDGE,"E17.2.3.1")])]})])],"derivedFrom":subQ6}),makeQuery(id+"F4.opExtrude","SWEPT_FACE",FACE,{"disambiguationData":[OSD([subQ0])]})]});}
            extrude(context, id + "F8", {"entities" : qUnion([Q0]), "operationType" : NewBodyOperationType.REMOVE, "endBound" : BoundingType.UP_TO_SURFACE, "oppositeDirection" : true, "depth" : 25 * mm, "endBoundEntityFace" : qUnion([Q1]), "offsetDistance" : 25 * mm});
        }
        {
            var Q0;
            Q0 = qSketchRegion(id + "F6", true);
            extrude(context, id + "F9", {"entities" : qUnion([Q0]), "operationType" : NewBodyOperationType.REMOVE, "oppositeDirection" : true, "depth" : 25 * mm, "offsetDistance" : 25 * mm, "symmetric" : true});
        }
    });
